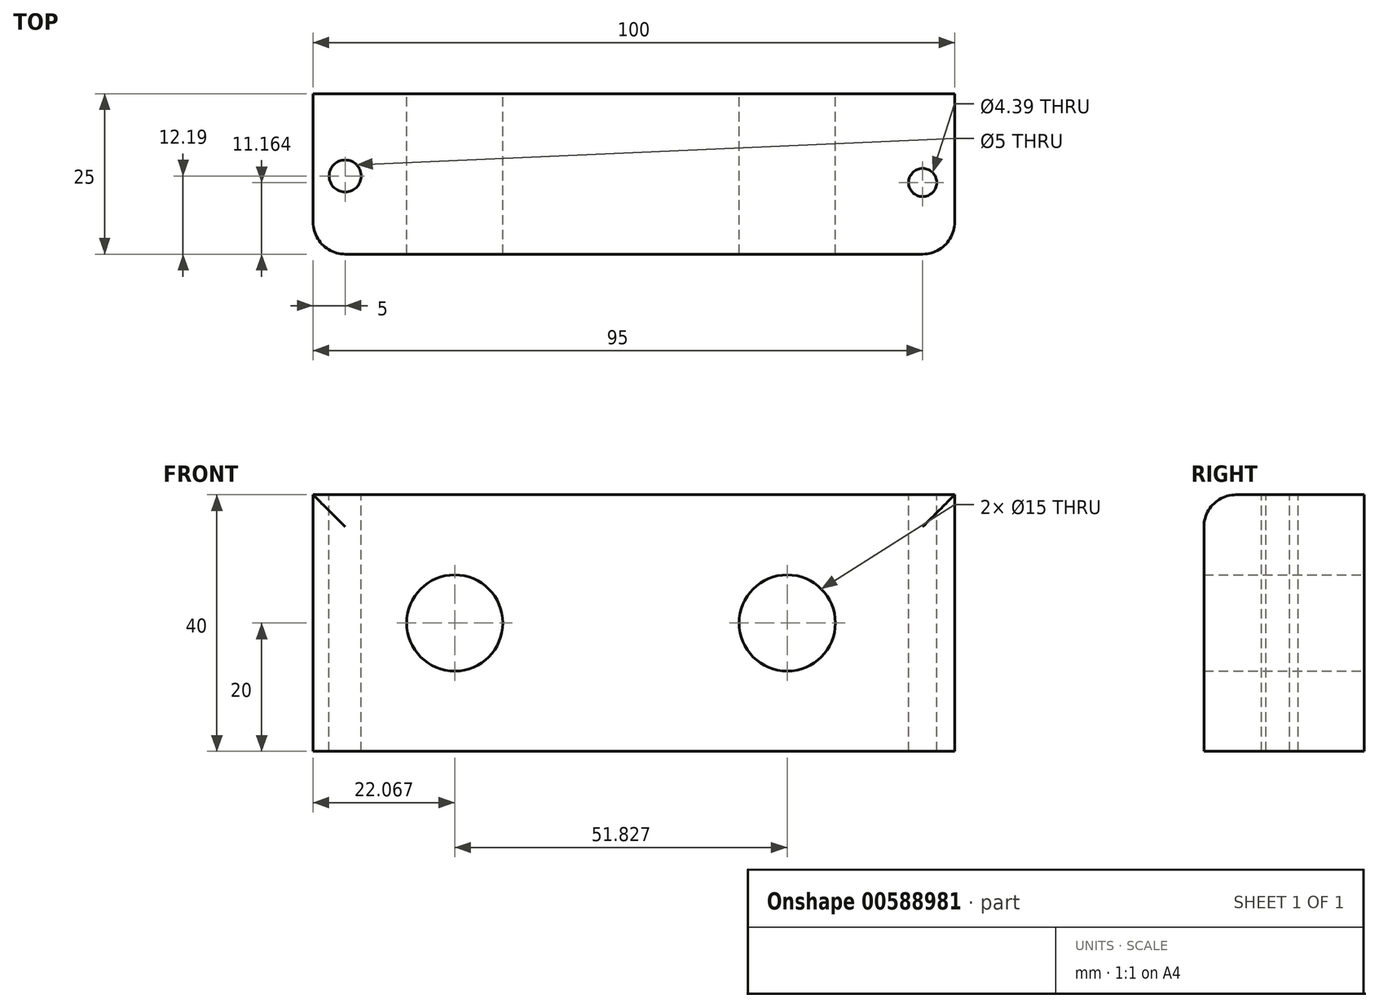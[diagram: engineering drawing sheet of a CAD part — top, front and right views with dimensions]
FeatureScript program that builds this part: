
annotation { "Feature Type Name" : "Feature", "Feature Type Description" : "" }
export const myFeature = defineFeature(function(context is Context, id is Id, definition is map)
    precondition{}
    {
        {
            var Q0;
            Q0=qCreatedBy(makeId("Front.planeOp"),FACE);
            var sketch = newSketch(context, id + "F0", { "sketchPlane" : qUnion([Q0])});
            skLineSegment(sketch, "E0.bottom", {"start": v(50, -20) * mm, "end": v(-50, -20) * mm});
            skLineSegment(sketch, "E0.top", {"start": v(50, 20) * mm, "end": v(-50, 20) * mm});
            skLineSegment(sketch, "E0.left", {"start": v(50, -20) * mm, "end": v(50, 20) * mm});
            skLineSegment(sketch, "E0.right", {"start": v(-50, -20) * mm, "end": v(-50, 20) * mm});
            skPoint(sketch, "E0.middle", {"position": v(0, 0) * mm});
            skCircle(sketch, "E1", {"center": v(-27.93, 0) * mm, "radius": 7.5 * mm});
            skCircle(sketch, "E2", {"center": v(23.9, 0) * mm, "radius": 7.5 * mm});
            skSolve(sketch);
        }
        {
            var Q0;
            Q0=makeQuery(id+"F0.imprint","IMPRINT",FACE,{"disambiguationData":[TD([[makeQuery(id+"F0.imprint","IMPRINT",EDGE,{"derivedFrom":sQuery(id+"F0.wireOp",EDGE,"E0.bottom")}),-1.0]])]});
            extrude(context, id + "F1", {"entities" : qUnion([Q0]), "depth" : 25 * mm, "offsetDistance" : 25 * mm});
        }
        {
            var Q0;
            Q0=makeQuery(id+"F1.opExtrude","SWEPT_FACE",FACE,{"disambiguationData":[OSD([sQuery(id+"F0.wireOp",EDGE,"E0.top")])]});
            var sketch = newSketch(context, id + "F2", { "sketchPlane" : qUnion([Q0])});
            skCircle(sketch, "E3", {"center": v(-45, -12.81) * mm, "radius": 2.5 * mm});
            skCircle(sketch, "E4", {"center": v(45, -13.84) * mm, "radius": 2.2 * mm});
            skSolve(sketch);
        }
        {
            var Q0;
            Q0=makeQuery(id+"F2.imprint","IMPRINT",FACE,{"disambiguationData":[TD([[makeQuery(id+"F2.imprint","IMPRINT",EDGE,{"derivedFrom":sQuery(id+"F2.wireOp",EDGE,"E3")}),1.0]])]});
            var Q1;
            Q1=makeQuery(id+"F2.imprint","IMPRINT",FACE,{"disambiguationData":[TD([[makeQuery(id+"F2.imprint","IMPRINT",EDGE,{"derivedFrom":sQuery(id+"F2.wireOp",EDGE,"E4")}),1.0]])]});
            extrude(context, id + "F3", {"entities" : qUnion([Q0, Q1]), "operationType" : NewBodyOperationType.REMOVE, "endBound" : BoundingType.THROUGH_ALL, "oppositeDirection" : true, "depth" : 25 * mm, "offsetDistance" : 25 * mm});
        }
        {
            var Q0;
            Q0=makeQuery(id+"F1.opExtrude","CAP_EDGE",EDGE,{"disambiguationData":[OSD([sQuery(id+"F0.wireOp",EDGE,"E0.right")])],"isStart":false});
            var Q1;
            Q1=makeQuery(id+"F1.opExtrude","CAP_EDGE",EDGE,{"disambiguationData":[OSD([sQuery(id+"F0.wireOp",EDGE,"E0.top")])],"isStart":false});
            var Q2;
            Q2=makeQuery(id+"F1.opExtrude","CAP_EDGE",EDGE,{"disambiguationData":[OSD([sQuery(id+"F0.wireOp",EDGE,"E0.left")])],"isStart":false});
            fillet(context, id + "F4", {"entities" : qUnion([Q0, Q1, Q2]), "radius" : 5 * mm, "tangentPropagation" : true, "allowEdgeOverflow" : false});
        }
    });
